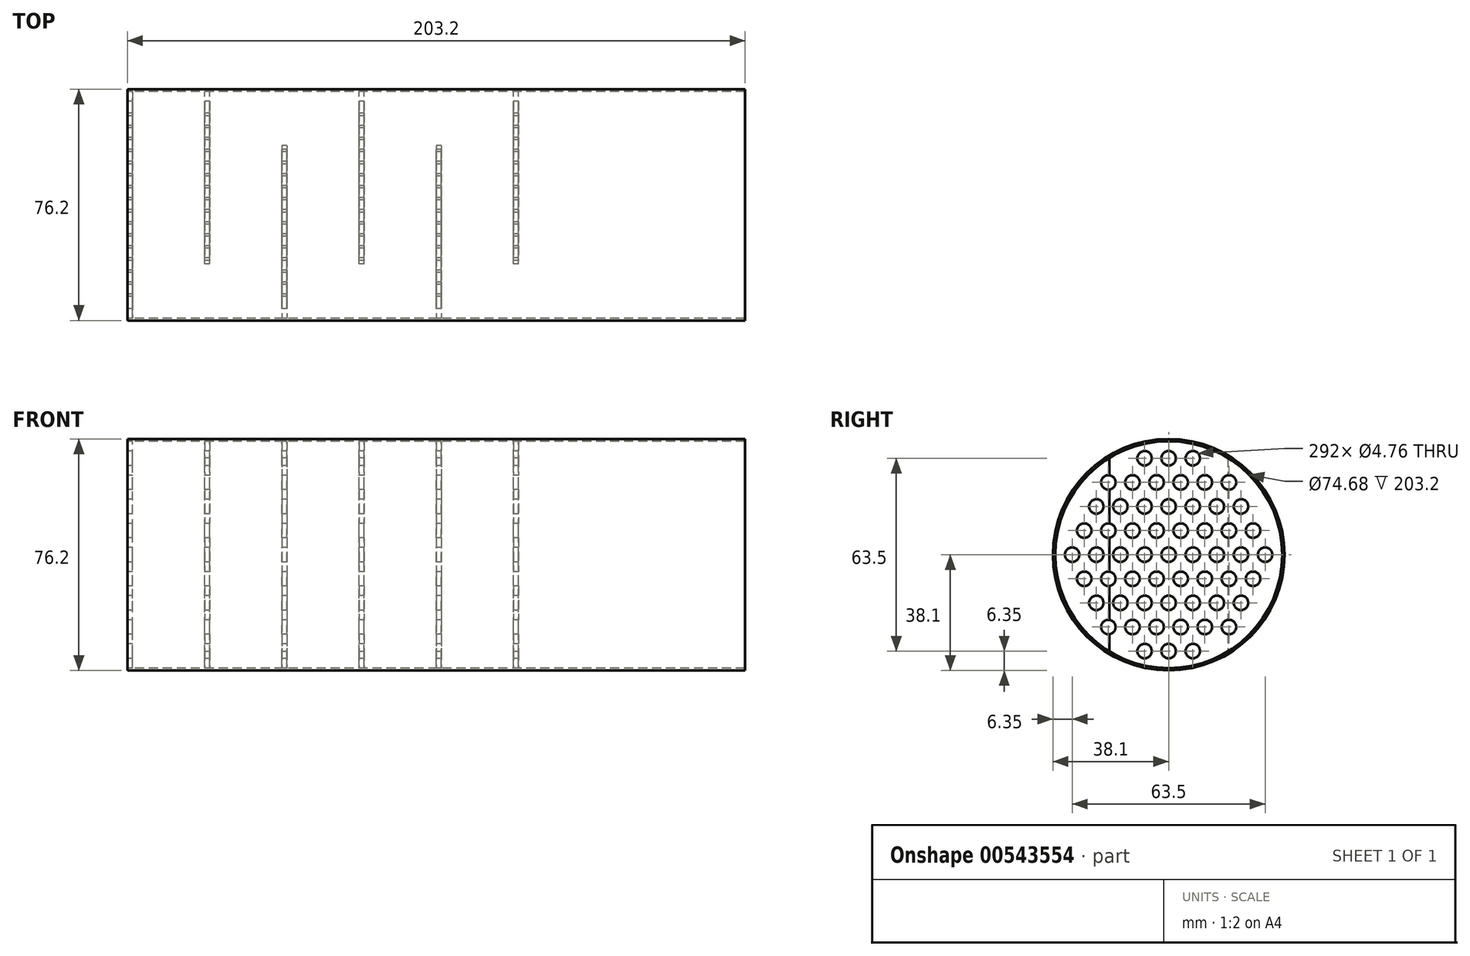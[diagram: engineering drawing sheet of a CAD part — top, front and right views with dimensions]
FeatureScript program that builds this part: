
annotation { "Feature Type Name" : "Feature", "Feature Type Description" : "" }
export const myFeature = defineFeature(function(context is Context, id is Id, definition is map)
    precondition{}
    {
        {
            var Q0;
            Q0=qCreatedBy(makeId("Right.planeOp"),FACE);
            var sketch = newSketch(context, id + "F0", { "sketchPlane" : qUnion([Q0])});
            skCircle(sketch, "E0", {"center": v(0, 0) * mm, "radius": 38.1 * mm});
            skCircle(sketch, "E1", {"center": v(0, 0) * mm, "radius": 37.34 * mm});
            skSolve(sketch);
        }
        {
            var Q0;
            Q0 = qSketchRegion(id + "F0", true);
            extrude(context, id + "F1", {"entities" : qUnion([Q0]), "depth" : 203.2 * mm, "offsetDistance" : 25.4 * mm});
        }
        {
            var Q0;
            Q0=qCreatedBy(makeId("Right.planeOp"),FACE);
            var sketch = newSketch(context, id + "F2", { "sketchPlane" : qUnion([Q0])});
            skCircle(sketch, "E2", {"center": v(0, 0) * mm, "radius": 37.34 * mm});
            skSolve(sketch);
        }
        {
            var Q0;
            Q0 = qSketchRegion(id + "F2", true);
            extrude(context, id + "F3", {"entities" : qUnion([Q0]), "depth" : 1.59 * mm, "offsetDistance" : 25.4 * mm});
        }
        {
            var Q0;
            Q0=qCreatedBy(makeId("Right.planeOp"),FACE);
            var sketch = newSketch(context, id + "F4", { "sketchPlane" : qUnion([Q0])});
            skCircle(sketch, "E3", {"center": v(0, 0) * mm, "radius": 2.38 * mm});
            skCircle(sketch, "E4", {"center": v(-7.94, 0) * mm, "radius": 2.38 * mm});
            skCircle(sketch, "E5", {"center": v(-15.88, 0) * mm, "radius": 2.38 * mm});
            skCircle(sketch, "E6", {"center": v(-23.81, 0) * mm, "radius": 2.38 * mm});
            skCircle(sketch, "E7", {"center": v(-31.75, 0) * mm, "radius": 2.38 * mm});
            skCircle(sketch, "E8", {"center": v(7.94, 0) * mm, "radius": 2.38 * mm});
            skCircle(sketch, "E9", {"center": v(31.75, 0) * mm, "radius": 2.38 * mm});
            skCircle(sketch, "E10", {"center": v(23.81, 0) * mm, "radius": 2.38 * mm});
            skCircle(sketch, "E11", {"center": v(15.88, 0) * mm, "radius": 2.38 * mm});
            skSolve(sketch);
        }
        {
            var Q0;
            Q0=qCreatedBy(makeId("Right.planeOp"),FACE);
            var sketch = newSketch(context, id + "F5", { "sketchPlane" : qUnion([Q0])});
            skCircle(sketch, "E12", {"center": v(-3.97, 7.94) * mm, "radius": 2.38 * mm});
            skCircle(sketch, "E13", {"center": v(-11.9, 7.94) * mm, "radius": 2.38 * mm});
            skCircle(sketch, "E14", {"center": v(-19.84, 7.94) * mm, "radius": 2.38 * mm});
            skCircle(sketch, "E15", {"center": v(-27.78, 7.94) * mm, "radius": 2.38 * mm});
            skCircle(sketch, "E16", {"center": v(3.97, 7.94) * mm, "radius": 2.38 * mm});
            skCircle(sketch, "E17", {"center": v(11.9, 7.94) * mm, "radius": 2.38 * mm});
            skCircle(sketch, "E18", {"center": v(27.78, 7.94) * mm, "radius": 2.38 * mm});
            skCircle(sketch, "E19", {"center": v(19.84, 7.94) * mm, "radius": 2.38 * mm});
            skCircle(sketch, "E20", {"center": v(27.78, -7.94) * mm, "radius": 2.38 * mm});
            skCircle(sketch, "E21", {"center": v(19.84, -7.94) * mm, "radius": 2.38 * mm});
            skCircle(sketch, "E22", {"center": v(11.9, -7.94) * mm, "radius": 2.38 * mm});
            skCircle(sketch, "E23", {"center": v(3.97, -7.94) * mm, "radius": 2.38 * mm});
            skCircle(sketch, "E24", {"center": v(-3.97, -7.94) * mm, "radius": 2.38 * mm});
            skCircle(sketch, "E25", {"center": v(-11.9, -7.94) * mm, "radius": 2.38 * mm});
            skCircle(sketch, "E26", {"center": v(-19.84, -7.94) * mm, "radius": 2.38 * mm});
            skCircle(sketch, "E27", {"center": v(-27.78, -7.94) * mm, "radius": 2.38 * mm});
            skSolve(sketch);
        }
        {
            var Q0;
            Q0=qCreatedBy(makeId("Right.planeOp"),FACE);
            var sketch = newSketch(context, id + "F6", { "sketchPlane" : qUnion([Q0])});
            skCircle(sketch, "E28", {"center": v(23.81, 15.88) * mm, "radius": 2.38 * mm});
            skCircle(sketch, "E29", {"center": v(15.87, 15.88) * mm, "radius": 2.38 * mm});
            skCircle(sketch, "E30", {"center": v(7.94, 15.88) * mm, "radius": 2.38 * mm});
            skCircle(sketch, "E31", {"center": v(0, 15.88) * mm, "radius": 2.38 * mm});
            skCircle(sketch, "E32", {"center": v(-7.94, 15.88) * mm, "radius": 2.38 * mm});
            skCircle(sketch, "E33", {"center": v(-15.88, 15.88) * mm, "radius": 2.38 * mm});
            skCircle(sketch, "E34", {"center": v(-23.81, 15.88) * mm, "radius": 2.38 * mm});
            skCircle(sketch, "E35", {"center": v(23.81, -15.88) * mm, "radius": 2.38 * mm});
            skCircle(sketch, "E36", {"center": v(15.88, -15.88) * mm, "radius": 2.38 * mm});
            skCircle(sketch, "E37", {"center": v(7.94, -15.88) * mm, "radius": 2.38 * mm});
            skCircle(sketch, "E38", {"center": v(0, -15.88) * mm, "radius": 2.38 * mm});
            skCircle(sketch, "E39", {"center": v(-7.94, -15.88) * mm, "radius": 2.38 * mm});
            skCircle(sketch, "E40", {"center": v(-15.88, -15.88) * mm, "radius": 2.38 * mm});
            skCircle(sketch, "E41", {"center": v(-23.81, -15.88) * mm, "radius": 2.38 * mm});
            skSolve(sketch);
        }
        {
            var Q0;
            Q0=qCreatedBy(makeId("Right.planeOp"),FACE);
            var sketch = newSketch(context, id + "F7", { "sketchPlane" : qUnion([Q0])});
            skCircle(sketch, "E42", {"center": v(19.84, 23.81) * mm, "radius": 2.38 * mm});
            skCircle(sketch, "E43", {"center": v(11.9, 23.81) * mm, "radius": 2.38 * mm});
            skCircle(sketch, "E44", {"center": v(3.97, 23.81) * mm, "radius": 2.38 * mm});
            skCircle(sketch, "E45", {"center": v(-3.97, 23.81) * mm, "radius": 2.38 * mm});
            skCircle(sketch, "E46", {"center": v(-11.9, 23.81) * mm, "radius": 2.38 * mm});
            skCircle(sketch, "E47", {"center": v(-19.84, 23.81) * mm, "radius": 2.38 * mm});
            skCircle(sketch, "E48", {"center": v(19.84, -23.81) * mm, "radius": 2.38 * mm});
            skCircle(sketch, "E49", {"center": v(11.9, -23.81) * mm, "radius": 2.38 * mm});
            skCircle(sketch, "E50", {"center": v(3.97, -23.81) * mm, "radius": 2.38 * mm});
            skCircle(sketch, "E51", {"center": v(-3.97, -23.81) * mm, "radius": 2.38 * mm});
            skCircle(sketch, "E52", {"center": v(-11.9, -23.81) * mm, "radius": 2.38 * mm});
            skCircle(sketch, "E53", {"center": v(-19.84, -23.81) * mm, "radius": 2.38 * mm});
            skSolve(sketch);
        }
        {
            var Q0;
            Q0=qCreatedBy(makeId("Right.planeOp"),FACE);
            var sketch = newSketch(context, id + "F8", { "sketchPlane" : qUnion([Q0])});
            skCircle(sketch, "E54", {"center": v(7.94, 31.75) * mm, "radius": 2.38 * mm});
            skCircle(sketch, "E55", {"center": v(0, 31.75) * mm, "radius": 2.38 * mm});
            skCircle(sketch, "E56", {"center": v(-7.94, 31.75) * mm, "radius": 2.38 * mm});
            skCircle(sketch, "E57", {"center": v(7.94, -31.75) * mm, "radius": 2.38 * mm});
            skCircle(sketch, "E58", {"center": v(0, -31.75) * mm, "radius": 2.38 * mm});
            skCircle(sketch, "E59", {"center": v(-7.94, -31.75) * mm, "radius": 2.38 * mm});
            skSolve(sketch);
        }
        {
            var Q0;
            Q0=qCreatedBy(makeId("Right.planeOp"),FACE);
            cPlane(context, id + "F9", {"entities" : qUnion([Q0]), "cplaneType" : CPlaneType.OFFSET, "offset" : 25.4 * mm, "width" : 152.4 * mm, "height" : 152.4 * mm});
        }
        {
            var Q0;
            Q0=qCreatedBy(id+"F9.planeOp",FACE);
            var sketch = newSketch(context, id + "F10", { "sketchPlane" : qUnion([Q0])});
            skArc(sketch, "E60", {"start": v(-19.5, -31.84) * mm, "mid": v(37.34, 0) * mm, "end": v(-19.5, 31.84) * mm});
            skLineSegment(sketch, "E61", {"start": v(-19.5, 31.84) * mm, "end": v(-19.5, -31.84) * mm});
            skSolve(sketch);
        }
        {
            var Q0;
            Q0 = qSketchRegion(id + "F10", true);
            extrude(context, id + "F11", {"entities" : qUnion([Q0]), "depth" : 1.59 * mm, "offsetDistance" : 25.4 * mm});
        }
        {
            var Q0;
            Q0=qCreatedBy(makeId("Right.planeOp"),FACE);
            cPlane(context, id + "F12", {"entities" : qUnion([Q0]), "cplaneType" : CPlaneType.OFFSET, "offset" : 50.8 * mm, "width" : 152.4 * mm, "height" : 152.4 * mm});
        }
        {
            var Q0;
            Q0=qCreatedBy(id+"F12.planeOp",FACE);
            var sketch = newSketch(context, id + "F13", { "sketchPlane" : qUnion([Q0])});
            skArc(sketch, "E62", {"start": v(19.5, 31.84) * mm, "mid": v(-37.34, 0) * mm, "end": v(19.5, -31.84) * mm});
            skLineSegment(sketch, "E63", {"start": v(19.5, 31.84) * mm, "end": v(19.5, -31.84) * mm});
            skSolve(sketch);
        }
        {
            var Q0;
            Q0 = qSketchRegion(id + "F13", true);
            extrude(context, id + "F14", {"entities" : qUnion([Q0]), "depth" : 1.59 * mm, "offsetDistance" : 25.4 * mm});
        }
        {
            var Q0;
            Q0=qCreatedBy(id+"F12.planeOp",FACE);
            cPlane(context, id + "F15", {"entities" : qUnion([Q0]), "cplaneType" : CPlaneType.OFFSET, "offset" : 25.4 * mm, "width" : 152.4 * mm, "height" : 152.4 * mm});
        }
        {
            var Q0;
            Q0=qCreatedBy(id+"F15.planeOp",FACE);
            var sketch = newSketch(context, id + "F16", { "sketchPlane" : qUnion([Q0])});
            skArc(sketch, "E64", {"start": v(-19.5, -31.84) * mm, "mid": v(37.34, 0) * mm, "end": v(-19.5, 31.84) * mm});
            skLineSegment(sketch, "E65", {"start": v(-19.5, 31.84) * mm, "end": v(-19.5, -31.84) * mm});
            skSolve(sketch);
        }
        {
            var Q0;
            Q0 = qSketchRegion(id + "F16", true);
            extrude(context, id + "F17", {"entities" : qUnion([Q0]), "depth" : 1.59 * mm, "offsetDistance" : 25.4 * mm});
        }
        {
            var Q0;
            Q0=qCreatedBy(id+"F15.planeOp",FACE);
            cPlane(context, id + "F18", {"entities" : qUnion([Q0]), "cplaneType" : CPlaneType.OFFSET, "offset" : 25.4 * mm, "width" : 152.4 * mm, "height" : 152.4 * mm});
        }
        {
            var Q0;
            Q0=qCreatedBy(id+"F18.planeOp",FACE);
            cPlane(context, id + "F19", {"entities" : qUnion([Q0]), "cplaneType" : CPlaneType.OFFSET, "offset" : 25.4 * mm, "width" : 152.4 * mm, "height" : 152.4 * mm});
        }
        {
            var Q0;
            Q0=qCreatedBy(id+"F19.planeOp",FACE);
            cPlane(context, id + "F20", {"entities" : qUnion([Q0]), "cplaneType" : CPlaneType.OFFSET, "offset" : 25.4 * mm, "width" : 152.4 * mm, "height" : 152.4 * mm});
        }
        {
            var Q0;
            Q0=qCreatedBy(id+"F20.planeOp",FACE);
            cPlane(context, id + "F21", {"entities" : qUnion([Q0]), "cplaneType" : CPlaneType.OFFSET, "offset" : 25.4 * mm, "width" : 152.4 * mm, "height" : 152.4 * mm});
        }
        {
            var Q0;
            Q0=qCreatedBy(id+"F18.planeOp",FACE);
            var sketch = newSketch(context, id + "F22", { "sketchPlane" : qUnion([Q0])});
            skArc(sketch, "E66", {"start": v(19.5, 31.84) * mm, "mid": v(-37.34, 0) * mm, "end": v(19.5, -31.84) * mm});
            skLineSegment(sketch, "E67", {"start": v(19.5, 31.84) * mm, "end": v(19.5, -31.84) * mm});
            skSolve(sketch);
        }
        {
            var Q0;
            Q0 = qSketchRegion(id + "F22", true);
            extrude(context, id + "F23", {"entities" : qUnion([Q0]), "depth" : 1.59 * mm, "offsetDistance" : 25.4 * mm});
        }
        {
            var Q0;
            Q0=qCreatedBy(id+"F19.planeOp",FACE);
            var sketch = newSketch(context, id + "F24", { "sketchPlane" : qUnion([Q0])});
            skArc(sketch, "E68", {"start": v(-19.5, -31.84) * mm, "mid": v(37.34, 0) * mm, "end": v(-19.5, 31.84) * mm});
            skLineSegment(sketch, "E69", {"start": v(-19.5, 31.84) * mm, "end": v(-19.5, -31.84) * mm});
            skSolve(sketch);
        }
        {
            var Q0;
            Q0 = qSketchRegion(id + "F24", true);
            extrude(context, id + "F25", {"entities" : qUnion([Q0]), "depth" : 1.59 * mm, "offsetDistance" : 25.4 * mm});
        }
        {
            var Q0;
            Q0=makeQuery(id+"F8.imprint","IMPRINT",FACE,{"disambiguationData":[TD([[makeQuery(id+"F8.imprint","IMPRINT",EDGE,{"derivedFrom":sQuery(id+"F8.wireOp",EDGE,"E54")}),1.0]])]});
            var Q1;
            Q1=makeQuery(id+"F8.imprint","IMPRINT",FACE,{"disambiguationData":[TD([[makeQuery(id+"F8.imprint","IMPRINT",EDGE,{"derivedFrom":sQuery(id+"F8.wireOp",EDGE,"E55")}),1.0]])]});
            var Q2;
            Q2=makeQuery(id+"F8.imprint","IMPRINT",FACE,{"disambiguationData":[TD([[makeQuery(id+"F8.imprint","IMPRINT",EDGE,{"derivedFrom":sQuery(id+"F8.wireOp",EDGE,"E56")}),1.0]])]});
            var Q3;
            Q3=makeQuery(id+"F7.imprint","IMPRINT",FACE,{"disambiguationData":[TD([[makeQuery(id+"F7.imprint","IMPRINT",EDGE,{"derivedFrom":sQuery(id+"F7.wireOp",EDGE,"E42")}),1.0]])]});
            var Q4;
            Q4=makeQuery(id+"F7.imprint","IMPRINT",FACE,{"disambiguationData":[TD([[makeQuery(id+"F7.imprint","IMPRINT",EDGE,{"derivedFrom":sQuery(id+"F7.wireOp",EDGE,"E43")}),1.0]])]});
            var Q5;
            Q5=makeQuery(id+"F7.imprint","IMPRINT",FACE,{"disambiguationData":[TD([[makeQuery(id+"F7.imprint","IMPRINT",EDGE,{"derivedFrom":sQuery(id+"F7.wireOp",EDGE,"E44")}),1.0]])]});
            var Q6;
            Q6=makeQuery(id+"F7.imprint","IMPRINT",FACE,{"disambiguationData":[TD([[makeQuery(id+"F7.imprint","IMPRINT",EDGE,{"derivedFrom":sQuery(id+"F7.wireOp",EDGE,"E45")}),1.0]])]});
            var Q7;
            Q7=makeQuery(id+"F7.imprint","IMPRINT",FACE,{"disambiguationData":[TD([[makeQuery(id+"F7.imprint","IMPRINT",EDGE,{"derivedFrom":sQuery(id+"F7.wireOp",EDGE,"E46")}),1.0]])]});
            var Q8;
            Q8=makeQuery(id+"F7.imprint","IMPRINT",FACE,{"disambiguationData":[TD([[makeQuery(id+"F7.imprint","IMPRINT",EDGE,{"derivedFrom":sQuery(id+"F7.wireOp",EDGE,"E47")}),1.0]])]});
            var Q9;
            Q9=makeQuery(id+"F6.imprint","IMPRINT",FACE,{"disambiguationData":[TD([[makeQuery(id+"F6.imprint","IMPRINT",EDGE,{"derivedFrom":sQuery(id+"F6.wireOp",EDGE,"E34")}),1.0]])]});
            var Q10;
            Q10=makeQuery(id+"F6.imprint","IMPRINT",FACE,{"disambiguationData":[TD([[makeQuery(id+"F6.imprint","IMPRINT",EDGE,{"derivedFrom":sQuery(id+"F6.wireOp",EDGE,"E33")}),1.0]])]});
            var Q11;
            Q11=makeQuery(id+"F6.imprint","IMPRINT",FACE,{"disambiguationData":[TD([[makeQuery(id+"F6.imprint","IMPRINT",EDGE,{"derivedFrom":sQuery(id+"F6.wireOp",EDGE,"E32")}),1.0]])]});
            var Q12;
            Q12=makeQuery(id+"F6.imprint","IMPRINT",FACE,{"disambiguationData":[TD([[makeQuery(id+"F6.imprint","IMPRINT",EDGE,{"derivedFrom":sQuery(id+"F6.wireOp",EDGE,"E31")}),1.0]])]});
            var Q13;
            Q13=makeQuery(id+"F6.imprint","IMPRINT",FACE,{"disambiguationData":[TD([[makeQuery(id+"F6.imprint","IMPRINT",EDGE,{"derivedFrom":sQuery(id+"F6.wireOp",EDGE,"E30")}),1.0]])]});
            var Q14;
            Q14=makeQuery(id+"F6.imprint","IMPRINT",FACE,{"disambiguationData":[TD([[makeQuery(id+"F6.imprint","IMPRINT",EDGE,{"derivedFrom":sQuery(id+"F6.wireOp",EDGE,"E29")}),1.0]])]});
            var Q15;
            Q15=makeQuery(id+"F6.imprint","IMPRINT",FACE,{"disambiguationData":[TD([[makeQuery(id+"F6.imprint","IMPRINT",EDGE,{"derivedFrom":sQuery(id+"F6.wireOp",EDGE,"E28")}),1.0]])]});
            var Q16;
            Q16=makeQuery(id+"F5.imprint","IMPRINT",FACE,{"disambiguationData":[TD([[makeQuery(id+"F5.imprint","IMPRINT",EDGE,{"derivedFrom":sQuery(id+"F5.wireOp",EDGE,"E18")}),1.0]])]});
            var Q17;
            Q17=makeQuery(id+"F5.imprint","IMPRINT",FACE,{"disambiguationData":[TD([[makeQuery(id+"F5.imprint","IMPRINT",EDGE,{"derivedFrom":sQuery(id+"F5.wireOp",EDGE,"E19")}),1.0]])]});
            var Q18;
            Q18=makeQuery(id+"F5.imprint","IMPRINT",FACE,{"disambiguationData":[TD([[makeQuery(id+"F5.imprint","IMPRINT",EDGE,{"derivedFrom":sQuery(id+"F5.wireOp",EDGE,"E17")}),1.0]])]});
            var Q19;
            Q19=makeQuery(id+"F5.imprint","IMPRINT",FACE,{"disambiguationData":[TD([[makeQuery(id+"F5.imprint","IMPRINT",EDGE,{"derivedFrom":sQuery(id+"F5.wireOp",EDGE,"E16")}),1.0]])]});
            var Q20;
            Q20=makeQuery(id+"F5.imprint","IMPRINT",FACE,{"disambiguationData":[TD([[makeQuery(id+"F5.imprint","IMPRINT",EDGE,{"derivedFrom":sQuery(id+"F5.wireOp",EDGE,"E12")}),1.0]])]});
            var Q21;
            Q21=makeQuery(id+"F5.imprint","IMPRINT",FACE,{"disambiguationData":[TD([[makeQuery(id+"F5.imprint","IMPRINT",EDGE,{"derivedFrom":sQuery(id+"F5.wireOp",EDGE,"E13")}),1.0]])]});
            var Q22;
            Q22=makeQuery(id+"F5.imprint","IMPRINT",FACE,{"disambiguationData":[TD([[makeQuery(id+"F5.imprint","IMPRINT",EDGE,{"derivedFrom":sQuery(id+"F5.wireOp",EDGE,"E14")}),1.0]])]});
            var Q23;
            Q23=makeQuery(id+"F5.imprint","IMPRINT",FACE,{"disambiguationData":[TD([[makeQuery(id+"F5.imprint","IMPRINT",EDGE,{"derivedFrom":sQuery(id+"F5.wireOp",EDGE,"E15")}),1.0]])]});
            var Q24;
            Q24=makeQuery(id+"F4.imprint","IMPRINT",FACE,{"disambiguationData":[TD([[makeQuery(id+"F4.imprint","IMPRINT",EDGE,{"derivedFrom":sQuery(id+"F4.wireOp",EDGE,"E9")}),1.0]])]});
            var Q25;
            Q25=makeQuery(id+"F4.imprint","IMPRINT",FACE,{"disambiguationData":[TD([[makeQuery(id+"F4.imprint","IMPRINT",EDGE,{"derivedFrom":sQuery(id+"F4.wireOp",EDGE,"E10")}),1.0]])]});
            var Q26;
            Q26=makeQuery(id+"F4.imprint","IMPRINT",FACE,{"disambiguationData":[TD([[makeQuery(id+"F4.imprint","IMPRINT",EDGE,{"derivedFrom":sQuery(id+"F4.wireOp",EDGE,"E11")}),1.0]])]});
            var Q27;
            Q27=makeQuery(id+"F4.imprint","IMPRINT",FACE,{"disambiguationData":[TD([[makeQuery(id+"F4.imprint","IMPRINT",EDGE,{"derivedFrom":sQuery(id+"F4.wireOp",EDGE,"E8")}),1.0]])]});
            var Q28;
            Q28=makeQuery(id+"F4.imprint","IMPRINT",FACE,{"disambiguationData":[TD([[makeQuery(id+"F4.imprint","IMPRINT",EDGE,{"derivedFrom":sQuery(id+"F4.wireOp",EDGE,"E3")}),1.0]])]});
            var Q29;
            Q29=makeQuery(id+"F4.imprint","IMPRINT",FACE,{"disambiguationData":[TD([[makeQuery(id+"F4.imprint","IMPRINT",EDGE,{"derivedFrom":sQuery(id+"F4.wireOp",EDGE,"E4")}),1.0]])]});
            var Q30;
            Q30=makeQuery(id+"F4.imprint","IMPRINT",FACE,{"disambiguationData":[TD([[makeQuery(id+"F4.imprint","IMPRINT",EDGE,{"derivedFrom":sQuery(id+"F4.wireOp",EDGE,"E5")}),1.0]])]});
            var Q31;
            Q31=makeQuery(id+"F4.imprint","IMPRINT",FACE,{"disambiguationData":[TD([[makeQuery(id+"F4.imprint","IMPRINT",EDGE,{"derivedFrom":sQuery(id+"F4.wireOp",EDGE,"E6")}),1.0]])]});
            var Q32;
            Q32=makeQuery(id+"F4.imprint","IMPRINT",FACE,{"disambiguationData":[TD([[makeQuery(id+"F4.imprint","IMPRINT",EDGE,{"derivedFrom":sQuery(id+"F4.wireOp",EDGE,"E7")}),1.0]])]});
            var Q33;
            Q33=makeQuery(id+"F5.imprint","IMPRINT",FACE,{"disambiguationData":[TD([[makeQuery(id+"F5.imprint","IMPRINT",EDGE,{"derivedFrom":sQuery(id+"F5.wireOp",EDGE,"E27")}),1.0]])]});
            var Q34;
            Q34=makeQuery(id+"F5.imprint","IMPRINT",FACE,{"disambiguationData":[TD([[makeQuery(id+"F5.imprint","IMPRINT",EDGE,{"derivedFrom":sQuery(id+"F5.wireOp",EDGE,"E26")}),1.0]])]});
            var Q35;
            Q35=makeQuery(id+"F5.imprint","IMPRINT",FACE,{"disambiguationData":[TD([[makeQuery(id+"F5.imprint","IMPRINT",EDGE,{"derivedFrom":sQuery(id+"F5.wireOp",EDGE,"E25")}),1.0]])]});
            var Q36;
            Q36=makeQuery(id+"F5.imprint","IMPRINT",FACE,{"disambiguationData":[TD([[makeQuery(id+"F5.imprint","IMPRINT",EDGE,{"derivedFrom":sQuery(id+"F5.wireOp",EDGE,"E24")}),1.0]])]});
            var Q37;
            Q37=makeQuery(id+"F5.imprint","IMPRINT",FACE,{"disambiguationData":[TD([[makeQuery(id+"F5.imprint","IMPRINT",EDGE,{"derivedFrom":sQuery(id+"F5.wireOp",EDGE,"E23")}),1.0]])]});
            var Q38;
            Q38=makeQuery(id+"F5.imprint","IMPRINT",FACE,{"disambiguationData":[TD([[makeQuery(id+"F5.imprint","IMPRINT",EDGE,{"derivedFrom":sQuery(id+"F5.wireOp",EDGE,"E22")}),1.0]])]});
            var Q39;
            Q39=makeQuery(id+"F5.imprint","IMPRINT",FACE,{"disambiguationData":[TD([[makeQuery(id+"F5.imprint","IMPRINT",EDGE,{"derivedFrom":sQuery(id+"F5.wireOp",EDGE,"E21")}),1.0]])]});
            var Q40;
            Q40=makeQuery(id+"F5.imprint","IMPRINT",FACE,{"disambiguationData":[TD([[makeQuery(id+"F5.imprint","IMPRINT",EDGE,{"derivedFrom":sQuery(id+"F5.wireOp",EDGE,"E20")}),1.0]])]});
            var Q41;
            Q41=makeQuery(id+"F6.imprint","IMPRINT",FACE,{"disambiguationData":[TD([[makeQuery(id+"F6.imprint","IMPRINT",EDGE,{"derivedFrom":sQuery(id+"F6.wireOp",EDGE,"E36")}),1.0]])]});
            var Q42;
            Q42=makeQuery(id+"F6.imprint","IMPRINT",FACE,{"disambiguationData":[TD([[makeQuery(id+"F6.imprint","IMPRINT",EDGE,{"derivedFrom":sQuery(id+"F6.wireOp",EDGE,"E37")}),1.0]])]});
            var Q43;
            Q43=makeQuery(id+"F6.imprint","IMPRINT",FACE,{"disambiguationData":[TD([[makeQuery(id+"F6.imprint","IMPRINT",EDGE,{"derivedFrom":sQuery(id+"F6.wireOp",EDGE,"E38")}),1.0]])]});
            var Q44;
            Q44=makeQuery(id+"F6.imprint","IMPRINT",FACE,{"disambiguationData":[TD([[makeQuery(id+"F6.imprint","IMPRINT",EDGE,{"derivedFrom":sQuery(id+"F6.wireOp",EDGE,"E39")}),1.0]])]});
            var Q45;
            Q45=makeQuery(id+"F6.imprint","IMPRINT",FACE,{"disambiguationData":[TD([[makeQuery(id+"F6.imprint","IMPRINT",EDGE,{"derivedFrom":sQuery(id+"F6.wireOp",EDGE,"E40")}),1.0]])]});
            var Q46;
            Q46=makeQuery(id+"F6.imprint","IMPRINT",FACE,{"disambiguationData":[TD([[makeQuery(id+"F6.imprint","IMPRINT",EDGE,{"derivedFrom":sQuery(id+"F6.wireOp",EDGE,"E41")}),1.0]])]});
            var Q47;
            Q47=makeQuery(id+"F7.imprint","IMPRINT",FACE,{"disambiguationData":[TD([[makeQuery(id+"F7.imprint","IMPRINT",EDGE,{"derivedFrom":sQuery(id+"F7.wireOp",EDGE,"E53")}),1.0]])]});
            var Q48;
            Q48=makeQuery(id+"F7.imprint","IMPRINT",FACE,{"disambiguationData":[TD([[makeQuery(id+"F7.imprint","IMPRINT",EDGE,{"derivedFrom":sQuery(id+"F7.wireOp",EDGE,"E52")}),1.0]])]});
            var Q49;
            Q49=makeQuery(id+"F7.imprint","IMPRINT",FACE,{"disambiguationData":[TD([[makeQuery(id+"F7.imprint","IMPRINT",EDGE,{"derivedFrom":sQuery(id+"F7.wireOp",EDGE,"E51")}),1.0]])]});
            var Q50;
            Q50=makeQuery(id+"F7.imprint","IMPRINT",FACE,{"disambiguationData":[TD([[makeQuery(id+"F7.imprint","IMPRINT",EDGE,{"derivedFrom":sQuery(id+"F7.wireOp",EDGE,"E50")}),1.0]])]});
            var Q51;
            Q51=makeQuery(id+"F7.imprint","IMPRINT",FACE,{"disambiguationData":[TD([[makeQuery(id+"F7.imprint","IMPRINT",EDGE,{"derivedFrom":sQuery(id+"F7.wireOp",EDGE,"E48")}),1.0]])]});
            var Q52;
            Q52=makeQuery(id+"F6.imprint","IMPRINT",FACE,{"disambiguationData":[TD([[makeQuery(id+"F6.imprint","IMPRINT",EDGE,{"derivedFrom":sQuery(id+"F6.wireOp",EDGE,"E35")}),1.0]])]});
            var Q53;
            Q53=makeQuery(id+"F8.imprint","IMPRINT",FACE,{"disambiguationData":[TD([[makeQuery(id+"F8.imprint","IMPRINT",EDGE,{"derivedFrom":sQuery(id+"F8.wireOp",EDGE,"E57")}),1.0]])]});
            var Q54;
            Q54=makeQuery(id+"F7.imprint","IMPRINT",FACE,{"disambiguationData":[TD([[makeQuery(id+"F7.imprint","IMPRINT",EDGE,{"derivedFrom":sQuery(id+"F7.wireOp",EDGE,"E49")}),1.0]])]});
            var Q55;
            Q55=makeQuery(id+"F8.imprint","IMPRINT",FACE,{"disambiguationData":[TD([[makeQuery(id+"F8.imprint","IMPRINT",EDGE,{"derivedFrom":sQuery(id+"F8.wireOp",EDGE,"E58")}),1.0]])]});
            var Q56;
            Q56=makeQuery(id+"F8.imprint","IMPRINT",FACE,{"disambiguationData":[TD([[makeQuery(id+"F8.imprint","IMPRINT",EDGE,{"derivedFrom":sQuery(id+"F8.wireOp",EDGE,"E59")}),1.0]])]});
            var Q57;
            Q57=makeQuery(id+"F1.opExtrude","CAP_FACE",FACE,{"disambiguationData":[OSD([sQuery(id+"F0.wireOp",EDGE,"E0"),sQuery(id+"F0.wireOp",EDGE,"E1")])],"isStart":false});
            var Q58;
            Q58=makeQuery(id+"F1.opExtrude","CAP_FACE",FACE,{"disambiguationData":[OSD([sQuery(id+"F0.wireOp",EDGE,"E0"),sQuery(id+"F0.wireOp",EDGE,"E1")])],"isStart":false});
            extrude(context, id + "F26", {"entities" : qUnion([Q0, Q1, Q2, Q3, Q4, Q5, Q6, Q7, Q8, Q9, Q10, Q11, Q12, Q13, Q14, Q15, Q16, Q17, Q18, Q19, Q20, Q21, Q22, Q23, Q24, Q25, Q26, Q27, Q28, Q29, Q30, Q31, Q32, Q33, Q34, Q35, Q36, Q37, Q38, Q39, Q40, Q41, Q42, Q43, Q44, Q45, Q46, Q47, Q48, Q49, Q50, Q51, Q52, Q53, Q54, Q55, Q56]), "operationType" : NewBodyOperationType.REMOVE, "endBound" : BoundingType.THROUGH_ALL, "depth" : 203.2 * mm, "endBoundEntityFace" : qUnion([Q57]), "offsetDistance" : 25.4 * mm});
        }
    });
